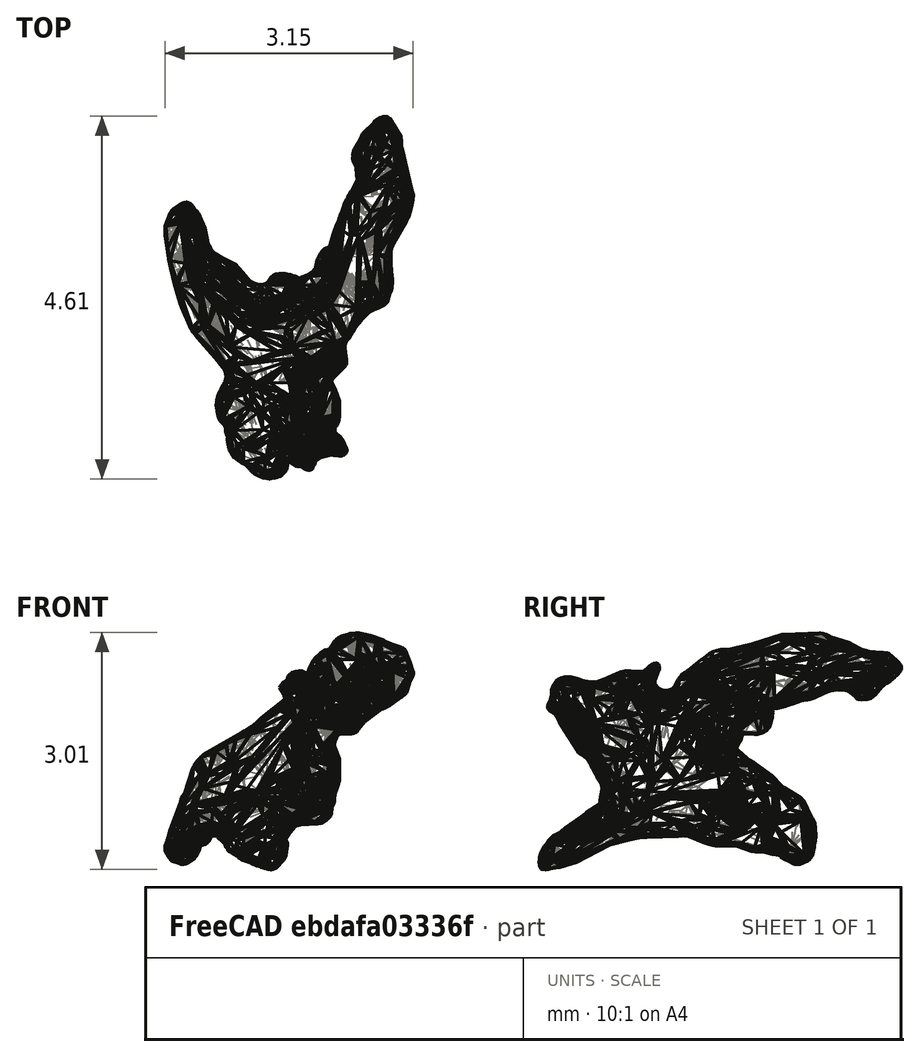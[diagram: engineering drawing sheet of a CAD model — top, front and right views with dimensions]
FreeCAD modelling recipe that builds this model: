
FCSTD DOCUMENT  (FreeCAD 0.20R29603 (Git))
Label: i_sclerite
License: All rights reserved
LicenseURL: http://en.wikipedia.org/wiki/All_rights_reserved
objects: Mesh::Feature×2, Part::Feature×1, PartDesign::FeatureBase×1, PartDesign::Point×1, PartDesign::Body×1
note: 4 computed .brp shape members not serialized (recipe doc carries the construction recipe); baked Part::Feature solids carry a one-line shape summary decoded from their .brp

FEATURE [Mesh::Feature] i_sclerite
FEATURE [Part::Feature] i_sclerite001
  shape: bbox 3.155 x 4.604 x 3.01 mm, 9460 faces, 0 solids (baked)
FEATURE [PartDesign::FeatureBase] BaseFeature
  BaseFeature = -> i_sclerite001
FEATURE [Mesh::Feature] sla
FEATURE [PartDesign::Point] DatumPoint  label="i_sclerite_DatumPoint"
  AttacherType = Attacher::AttachEnginePoint
  AttachmentOffset = pos=(-0.1,1.1,3.8) rot=(0,0,1;0rad)
  MapMode = 32
  Placement = pos=(-0.1,1.1,3.8) rot=(0,0,1;0rad)
  Support = -> [XY_Plane]
FEATURE [PartDesign::Body] Body  label="i_sclerite_Body"
  BaseFeature = -> i_sclerite001
  Group = -> [BaseFeature,DatumPoint]
  Origin = -> Origin
  Tip = -> BaseFeature
